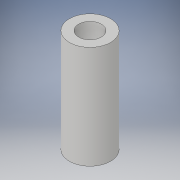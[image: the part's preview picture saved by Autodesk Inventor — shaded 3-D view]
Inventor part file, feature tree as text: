
AUTODESK INVENTOR PART (.ipt)
format: ipt  version: 2018 (Build 220112000, 112)  size: 98,304 bytes
history: native  units: in
note: dims shown in document units (in); Inventor stores cm internally (conversion verified against a paired STEP export)
features: sketch x2, extrude x1, hole x1
ambient origin geometry x8: Origin, YZ Plane, XZ Plane, XY Plane, X Axis, Y Axis, Z Axis, Center Point
bodies: Solid1 (feature_tree)
feature tree (4):
  extrude  "Extrusion1"  Depth=0.5in TaperAngle=0.0deg
  hole  "Hole1"  [1 undecoded]
  sketch  "Sketch1"  dims[d0=0.2in d1=0.5in d2=0.0in]
  sketch  "Sketch2"  dims[d3=0.11in d4=0.11in d5=0.75in d6=0.375in d7=0.25in d8=0.5635in d9=1.0in d10=0.8108in]
note: 1 required parameter value undecoded (feature->parameter linkage not recoverable at this tier; creation-order binding heuristic only, values carry confidence <= 0.55)
